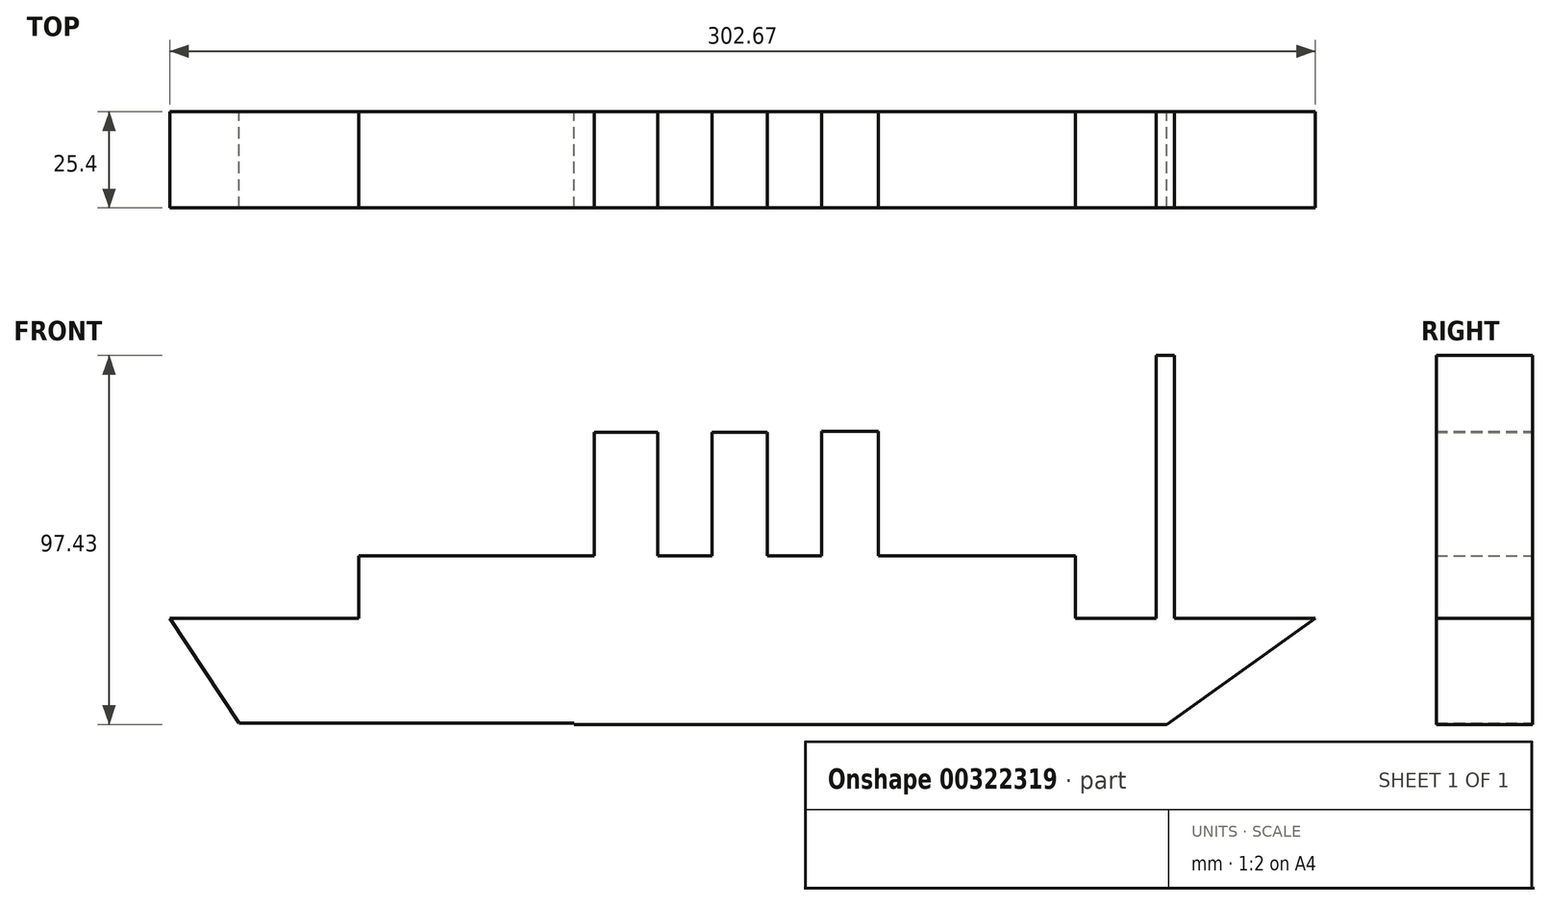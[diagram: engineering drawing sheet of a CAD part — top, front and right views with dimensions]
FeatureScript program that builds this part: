
annotation { "Feature Type Name" : "Feature", "Feature Type Description" : "" }
export const myFeature = defineFeature(function(context is Context, id is Id, definition is map)
    precondition{}
    {
        {
            var Q0;
            Q0=qCreatedBy(makeId("Front.planeOp"),FACE);
            var sketch = newSketch(context, id + "F0", { "sketchPlane" : qUnion([Q0])});
            skLineSegment(sketch, "E0.bottom", {"start": v(-144.54, -1.68) * mm, "end": v(12.13, -1.68) * mm});
            skLineSegment(sketch, "E0.top", {"start": v(-144.54, -29.72) * mm, "end": v(12.13, -29.72) * mm});
            skLineSegment(sketch, "E0.left", {"start": v(-144.54, -1.68) * mm, "end": v(-144.54, -29.72) * mm});
            skLineSegment(sketch, "E0.right", {"start": v(12.13, -1.68) * mm, "end": v(12.13, -29.72) * mm});
            skLineSegment(sketch, "E1.bottom", {"start": v(-144.54, -1.68) * mm, "end": v(-233.05, -1.68) * mm});
            skLineSegment(sketch, "E1.top", {"start": v(-144.54, -29.41) * mm, "end": v(-233.05, -29.41) * mm});
            skLineSegment(sketch, "E1.left", {"start": v(-144.54, -1.68) * mm, "end": v(-144.54, -29.41) * mm});
            skLineSegment(sketch, "E1.right", {"start": v(-233.05, -1.68) * mm, "end": v(-233.05, -29.41) * mm});
            skLineSegment(sketch, "E2", {"start": v(-233.05, -1.68) * mm, "end": v(-251.34, -1.68) * mm});
            skLineSegment(sketch, "E3", {"start": v(-251.34, -1.68) * mm, "end": v(-233.05, -29.41) * mm});
            skLineSegment(sketch, "E4", {"start": v(12.13, -1.68) * mm, "end": v(51.33, -1.68) * mm});
            skLineSegment(sketch, "E5", {"start": v(51.33, -1.68) * mm, "end": v(12.13, -29.72) * mm});
            skLineSegment(sketch, "E6.bottom", {"start": v(-201.35, 14.78) * mm, "end": v(-12.07, 14.78) * mm});
            skLineSegment(sketch, "E6.top", {"start": v(-201.35, -1.68) * mm, "end": v(-12.07, -1.68) * mm});
            skLineSegment(sketch, "E6.left", {"start": v(-201.35, 14.78) * mm, "end": v(-201.35, -1.68) * mm});
            skLineSegment(sketch, "E6.right", {"start": v(-12.07, 14.78) * mm, "end": v(-12.07, -1.68) * mm});
            skLineSegment(sketch, "E7.bottom", {"start": v(-171.48, 14.78) * mm, "end": v(-154.72, 14.78) * mm});
            skLineSegment(sketch, "E7.top", {"start": v(-171.48, 46.48) * mm, "end": v(-154.72, 46.48) * mm});
            skLineSegment(sketch, "E7.left", {"start": v(-171.48, 14.78) * mm, "end": v(-171.48, 46.48) * mm});
            skLineSegment(sketch, "E7.right", {"start": v(-154.72, 14.78) * mm, "end": v(-154.72, 46.48) * mm});
            skLineSegment(sketch, "E8.bottom", {"start": v(-139.17, 47.4) * mm, "end": v(-122.4, 47.4) * mm});
            skLineSegment(sketch, "E8.top", {"start": v(-139.17, 14.78) * mm, "end": v(-122.4, 14.78) * mm});
            skLineSegment(sketch, "E8.left", {"start": v(-139.17, 47.4) * mm, "end": v(-139.17, 14.78) * mm});
            skLineSegment(sketch, "E8.right", {"start": v(-122.4, 47.4) * mm, "end": v(-122.4, 14.78) * mm});
            skLineSegment(sketch, "E9.bottom", {"start": v(-108.08, 47.4) * mm, "end": v(-93.45, 47.4) * mm});
            skLineSegment(sketch, "E9.top", {"start": v(-108.08, 14.78) * mm, "end": v(-93.45, 14.78) * mm});
            skLineSegment(sketch, "E9.left", {"start": v(-108.08, 47.4) * mm, "end": v(-108.08, 14.78) * mm});
            skLineSegment(sketch, "E9.right", {"start": v(-93.45, 47.4) * mm, "end": v(-93.45, 14.78) * mm});
            skLineSegment(sketch, "E10.bottom", {"start": v(-79.03, 47.67) * mm, "end": v(-64.14, 47.67) * mm});
            skLineSegment(sketch, "E10.top", {"start": v(-79.03, 14.78) * mm, "end": v(-64.14, 14.78) * mm});
            skLineSegment(sketch, "E10.left", {"start": v(-79.03, 47.67) * mm, "end": v(-79.03, 14.78) * mm});
            skLineSegment(sketch, "E10.right", {"start": v(-64.14, 47.67) * mm, "end": v(-64.14, 14.78) * mm});
            skLineSegment(sketch, "E11.bottom", {"start": v(-233.05, -1.68) * mm, "end": v(-228.65, -1.68) * mm});
            skLineSegment(sketch, "E11.top", {"start": v(-233.05, 65.8) * mm, "end": v(-228.65, 65.8) * mm});
            skLineSegment(sketch, "E11.left", {"start": v(-233.05, -1.68) * mm, "end": v(-233.05, 65.8) * mm});
            skLineSegment(sketch, "E11.right", {"start": v(-228.65, -1.68) * mm, "end": v(-228.65, 65.8) * mm});
            skLineSegment(sketch, "E12.bottom", {"start": v(14.2, -1.68) * mm, "end": v(9.29, -1.68) * mm});
            skLineSegment(sketch, "E12.top", {"start": v(14.2, 67.7) * mm, "end": v(9.29, 67.7) * mm});
            skLineSegment(sketch, "E12.left", {"start": v(14.2, -1.68) * mm, "end": v(14.2, 67.7) * mm});
            skLineSegment(sketch, "E12.right", {"start": v(9.29, -1.68) * mm, "end": v(9.29, 67.7) * mm});
            skSolve(sketch);
        }
        {
            var Q0;
            {var subQ2=sQuery(id+"F0.wireOp",EDGE,"E1.bottom");Q0=makeQuery(id+"F0.imprint","IMPRINT",FACE,{"disambiguationData":[TD([[makeQuery(id+"F0.imprint","IMPRINT",EDGE,{"derivedFrom":subQ2}),1.0]])]});}
            var Q1;
            Q1=makeQuery(id+"F0.imprint","IMPRINT",FACE,{"disambiguationData":[TD([[makeQuery(id+"F0.imprint","IMPRINT",EDGE,{"derivedFrom":sQuery(id+"F0.wireOp",EDGE,"E1.right")}),-1.0]])]});
            var Q2;
            {var subQ2=sQuery(id+"F0.wireOp",EDGE,"E6.left");Q2=makeQuery(id+"F0.imprint","IMPRINT",FACE,{"disambiguationData":[TD([[makeQuery(id+"F0.imprint","IMPRINT",EDGE,{"derivedFrom":subQ2}),1.0]])]});}
            var Q3;
            Q3=makeQuery(id+"F0.imprint","IMPRINT",FACE,{"disambiguationData":[TD([[makeQuery(id+"F0.imprint","IMPRINT",EDGE,{"derivedFrom":sQuery(id+"F0.wireOp",EDGE,"E11.bottom")}),1.0]])]});
            var Q4;
            Q4=makeQuery(id+"F0.imprint","IMPRINT",FACE,{"disambiguationData":[TD([[makeQuery(id+"F0.imprint","IMPRINT",EDGE,{"derivedFrom":sQuery(id+"F0.wireOp",EDGE,"E7.bottom")}),1.0]])]});
            var Q5;
            Q5=makeQuery(id+"F0.imprint","IMPRINT",FACE,{"disambiguationData":[TD([[makeQuery(id+"F0.imprint","IMPRINT",EDGE,{"derivedFrom":sQuery(id+"F0.wireOp",EDGE,"E8.bottom")}),-1.0]])]});
            var Q6;
            Q6=makeQuery(id+"F0.imprint","IMPRINT",FACE,{"disambiguationData":[TD([[makeQuery(id+"F0.imprint","IMPRINT",EDGE,{"derivedFrom":sQuery(id+"F0.wireOp",EDGE,"E9.bottom")}),-1.0]])]});
            var Q7;
            Q7=makeQuery(id+"F0.imprint","IMPRINT",FACE,{"disambiguationData":[TD([[makeQuery(id+"F0.imprint","IMPRINT",EDGE,{"derivedFrom":sQuery(id+"F0.wireOp",EDGE,"E10.bottom")}),-1.0]])]});
            var Q8;
            {var subQ1=sQuery(id+"F0.wireOp",EDGE,"E0.bottom");Q8=makeQuery(id+"F0.imprint","IMPRINT",FACE,{"disambiguationData":[TD([[makeQuery(id+"F0.imprint","IMPRINT",EDGE,{"derivedFrom":subQ1}),-1.0]])]});}
            var Q9;
            {var subQ0=sQuery(id+"F0.wireOp",EDGE,"E0.right");Q9=makeQuery(id+"F0.imprint","IMPRINT",FACE,{"disambiguationData":[TD([[makeQuery(id+"F0.imprint","IMPRINT",EDGE,{"derivedFrom":subQ0}),1.0]])]});}
            var Q10;
            Q10=makeQuery(id+"F0.imprint","IMPRINT",FACE,{"disambiguationData":[TD([[makeQuery(id+"F0.imprint","IMPRINT",EDGE,{"derivedFrom":sQuery(id+"F0.wireOp",EDGE,"E12.top")}),1.0]])]});
            extrude(context, id + "F1", {"entities" : qUnion([Q0, Q1, Q2, Q3, Q4, Q5, Q6, Q7, Q8, Q9, Q10]), "depth" : 25.4 * mm});
        }
    });
